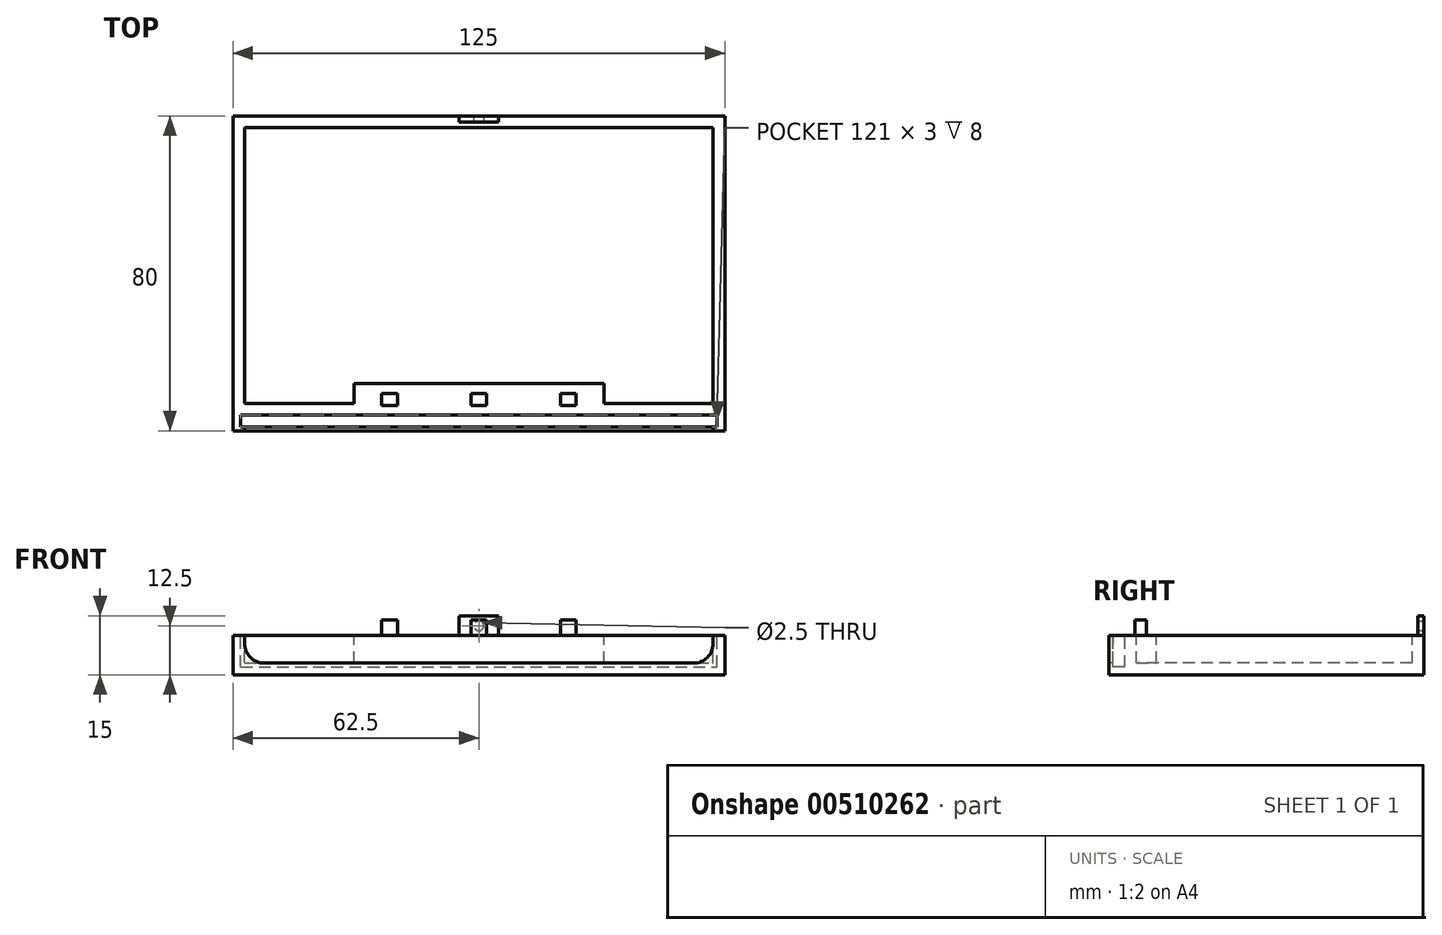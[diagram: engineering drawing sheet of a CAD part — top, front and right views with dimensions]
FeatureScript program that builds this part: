
annotation { "Feature Type Name" : "Feature", "Feature Type Description" : "" }
export const myFeature = defineFeature(function(context is Context, id is Id, definition is map)
    precondition{}
    {
        {
            var Q0;
            Q0=qCreatedBy(makeId("Top.planeOp"),FACE);
            var sketch = newSketch(context, id + "F0", { "sketchPlane" : qUnion([Q0])});
            skLineSegment(sketch, "E0.bottom", {"start": v(62.5, 40) * mm, "end": v(-62.5, 40) * mm});
            skLineSegment(sketch, "E0.top", {"start": v(62.5, -40) * mm, "end": v(-62.5, -40) * mm});
            skLineSegment(sketch, "E0.left", {"start": v(62.5, 40) * mm, "end": v(62.5, -40) * mm});
            skLineSegment(sketch, "E0.right", {"start": v(-62.5, 40) * mm, "end": v(-62.5, -40) * mm});
            skPoint(sketch, "E0.middle", {"position": v(0, 0) * mm});
            skSolve(sketch);
        }
        {
            var Q0;
            Q0 = qSketchRegion(id + "F0", true);
            extrude(context, id + "F1", {"entities" : qUnion([Q0]), "depth" : 10 * mm});
        }
        {
            var Q0;
            Q0=makeQuery(id+"F1.opExtrude","CAP_FACE",FACE,{"disambiguationData":[OSD([sQuery(id+"F0.wireOp",EDGE,"E0.bottom"),sQuery(id+"F0.wireOp",EDGE,"E0.top"),sQuery(id+"F0.wireOp",EDGE,"E0.left"),sQuery(id+"F0.wireOp",EDGE,"E0.right")])],"isStart":false});
            var sketch = newSketch(context, id + "F2", { "sketchPlane" : qUnion([Q0])});
            skLineSegment(sketch, "E1", {"start": v(-59.5, 37) * mm, "end": v(59.5, 37) * mm});
            skLineSegment(sketch, "E2", {"start": v(-59.5, 37) * mm, "end": v(-59.5, -33) * mm});
            skLineSegment(sketch, "E3", {"start": v(-59.5, -33) * mm, "end": v(-31.72, -33) * mm});
            skLineSegment(sketch, "E4", {"start": v(-31.72, -33) * mm, "end": v(-31.72, -28) * mm});
            skLineSegment(sketch, "E5", {"start": v(-31.72, -28) * mm, "end": v(31.72, -28) * mm});
            skLineSegment(sketch, "E6", {"start": v(31.72, -28) * mm, "end": v(31.72, -33) * mm});
            skLineSegment(sketch, "E7", {"start": v(31.72, -33) * mm, "end": v(59.5, -33) * mm});
            skLineSegment(sketch, "E8", {"start": v(59.5, -33) * mm, "end": v(59.5, 37) * mm});
            skSolve(sketch);
        }
        {
            var Q0;
            Q0 = qSketchRegion(id + "F2", true);
            extrude(context, id + "F3", {"entities" : qUnion([Q0]), "operationType" : NewBodyOperationType.REMOVE, "oppositeDirection" : true, "depth" : (10 - 3) * mm});
        }
        {
            var Q0;
            Q0=makeQuery(id+"F1.opExtrude","CAP_FACE",FACE,{"disambiguationData":[OSD([sQuery(id+"F0.wireOp",EDGE,"E0.bottom"),sQuery(id+"F0.wireOp",EDGE,"E0.top"),sQuery(id+"F0.wireOp",EDGE,"E0.left"),sQuery(id+"F0.wireOp",EDGE,"E0.right")])],"isStart":false});
            var sketch = newSketch(context, id + "F4", { "sketchPlane" : qUnion([Q0])});
            skLineSegment(sketch, "E9.bottom", {"start": v(-5, 38.5) * mm, "end": v(5, 38.5) * mm});
            skPoint(sketch, "E9.middle", {"position": v(0, 40) * mm});
            skLineSegment(sketch, "E10", {"start": v(-5, 38.5) * mm, "end": v(-5, 40) * mm});
            skLineSegment(sketch, "E11", {"start": v(5, 38.5) * mm, "end": v(5, 40) * mm});
            skLineSegment(sketch, "E12", {"start": v(5, 40) * mm, "end": v(-5, 40) * mm});
            skSolve(sketch);
        }
        {
            var Q0;
            Q0 = qSketchRegion(id + "F4", true);
            extrude(context, id + "F5", {"entities" : qUnion([Q0]), "operationType" : NewBodyOperationType.ADD, "depth" : 5 * mm});
        }
        {
            var Q0;
            Q0=makeQuery(id+"F5.boolean.opBoolean","MERGE",FACE,{"derivedFrom":[makeQuery(id+"F1.opExtrude","SWEPT_FACE",FACE,{"disambiguationData":[OSD([sQuery(id+"F0.wireOp",EDGE,"E0.bottom")])]}),makeQuery(id+"F5.opExtrude","SWEPT_FACE",FACE,{"disambiguationData":[OSD([sQuery(id+"F4.wireOp",EDGE,"E12")])]})]});
            var sketch = newSketch(context, id + "F6", { "sketchPlane" : qUnion([Q0])});
            skCircle(sketch, "E13", {"center": v(0, 12.5) * mm, "radius": 1.25 * mm});
            skSolve(sketch);
        }
        {
            var Q0;
            Q0 = qSketchRegion(id + "F6", true);
            extrude(context, id + "F7", {"entities" : qUnion([Q0]), "operationType" : NewBodyOperationType.REMOVE, "oppositeDirection" : true, "depth" : 25 * mm});
        }
        {
            var Q0;
            Q0=makeQuery(id+"F1.opExtrude","CAP_FACE",FACE,{"disambiguationData":[OSD([sQuery(id+"F0.wireOp",EDGE,"E0.bottom"),sQuery(id+"F0.wireOp",EDGE,"E0.top"),sQuery(id+"F0.wireOp",EDGE,"E0.left"),sQuery(id+"F0.wireOp",EDGE,"E0.right")])],"isStart":false});
            var sketch = newSketch(context, id + "F8", { "sketchPlane" : qUnion([Q0])});
            skLineSegment(sketch, "E14.bottom", {"start": v(-2, -33.5) * mm, "end": v(2, -33.5) * mm});
            skLineSegment(sketch, "E14.top", {"start": v(-2, -30.5) * mm, "end": v(2, -30.5) * mm});
            skLineSegment(sketch, "E14.left", {"start": v(-2, -33.5) * mm, "end": v(-2, -30.5) * mm});
            skLineSegment(sketch, "E14.right", {"start": v(2, -33.5) * mm, "end": v(2, -30.5) * mm});
            skPoint(sketch, "E14.middle", {"position": v(0, -32) * mm});
            skPoint(sketch, "E14.middle.positionSnap0", {"position": v(0, -28) * mm});
            skPoint(sketch, "E14.centerSnap0", {"position": v(0, -28) * mm});
            skLineSegment(sketch, "E15.bottom", {"start": v(24.72, -33.5) * mm, "end": v(20.72, -33.5) * mm});
            skLineSegment(sketch, "E15.top", {"start": v(24.72, -30.5) * mm, "end": v(20.72, -30.5) * mm});
            skLineSegment(sketch, "E15.left", {"start": v(24.72, -33.5) * mm, "end": v(24.72, -30.5) * mm});
            skLineSegment(sketch, "E15.right", {"start": v(20.72, -33.5) * mm, "end": v(20.72, -30.5) * mm});
            skPoint(sketch, "E15.middle", {"position": v(22.72, -32) * mm});
            skLineSegment(sketch, "E16.bottom", {"start": v(-20.72, -33.5) * mm, "end": v(-24.72, -33.5) * mm});
            skLineSegment(sketch, "E16.top", {"start": v(-20.72, -30.5) * mm, "end": v(-24.72, -30.5) * mm});
            skLineSegment(sketch, "E16.left", {"start": v(-20.72, -33.5) * mm, "end": v(-20.72, -30.5) * mm});
            skLineSegment(sketch, "E16.right", {"start": v(-24.72, -33.5) * mm, "end": v(-24.72, -30.5) * mm});
            skPoint(sketch, "E16.middle", {"position": v(-22.72, -32) * mm});
            skSolve(sketch);
        }
        {
            var Q0;
            Q0 = qSketchRegion(id + "F8", true);
            extrude(context, id + "F9", {"entities" : qUnion([Q0]), "operationType" : NewBodyOperationType.ADD, "depth" : 4 * mm});
        }
        {
            var Q0;
            Q0=makeQuery(id+"F1.opExtrude","SWEPT_FACE",FACE,{"disambiguationData":[OSD([sQuery(id+"F0.wireOp",EDGE,"E0.top")])]});
            var sketch = newSketch(context, id + "F10", { "sketchPlane" : qUnion([Q0])});
            skLineSegment(sketch, "E17", {"start": v(59.5, 7.95) * mm, "end": v(59.5, 10) * mm});
            skLineSegment(sketch, "E18", {"start": v(0, 10) * mm, "end": v(59.5, 10) * mm});
            skArc(sketch, "E19", {"start": v(54.55, 3) * mm, "mid": v(58.05, 4.45) * mm, "end": v(59.5, 7.95) * mm});
            skLineSegment(sketch, "E20", {"start": v(54.55, 3) * mm, "end": v(0, 3) * mm});
            skLineSegment(sketch, "E21.MirrorCS", {"start": v(-54.55, 3) * mm, "end": v(0, 3) * mm});
            skLineSegment(sketch, "E22.MirrorCS", {"start": v(0, 10) * mm, "end": v(-59.5, 10) * mm});
            skArc(sketch, "E23.MirrorCS", {"start": v(-54.55, 3) * mm, "mid": v(-58.05, 4.45) * mm, "end": v(-59.5, 7.95) * mm});
            skLineSegment(sketch, "E24.MirrorCS", {"start": v(-59.5, 7.95) * mm, "end": v(-59.5, 10) * mm});
            skSolve(sketch);
        }
        {
            var Q0;
            Q0 = qSketchRegion(id + "F10", true);
            extrude(context, id + "F11", {"entities" : qUnion([Q0]), "operationType" : NewBodyOperationType.REMOVE, "oppositeDirection" : true, "depth" : 4 * mm});
        }
        {
            var Q0;
            Q0=makeQuery(id+"F1.opExtrude","CAP_FACE",FACE,{"disambiguationData":[OSD([sQuery(id+"F0.wireOp",EDGE,"E0.bottom"),sQuery(id+"F0.wireOp",EDGE,"E0.top"),sQuery(id+"F0.wireOp",EDGE,"E0.left"),sQuery(id+"F0.wireOp",EDGE,"E0.right")])],"isStart":false});
            var sketch = newSketch(context, id + "F12", { "sketchPlane" : qUnion([Q0])});
            skLineSegment(sketch, "E25.bottom", {"start": v(-60.5, -36) * mm, "end": v(60.5, -36) * mm});
            skLineSegment(sketch, "E25.top", {"start": v(-60.5, -39) * mm, "end": v(60.5, -39) * mm});
            skLineSegment(sketch, "E25.left", {"start": v(-60.5, -36) * mm, "end": v(-60.5, -39) * mm});
            skLineSegment(sketch, "E25.right", {"start": v(60.5, -36) * mm, "end": v(60.5, -39) * mm});
            skPoint(sketch, "E25.middle", {"position": v(0, -37.5) * mm});
            skSolve(sketch);
        }
        {
            var Q0;
            Q0 = qSketchRegion(id + "F12", true);
            extrude(context, id + "F13", {"entities" : qUnion([Q0]), "operationType" : NewBodyOperationType.REMOVE, "oppositeDirection" : true, "depth" : 8 * mm});
        }
    });
